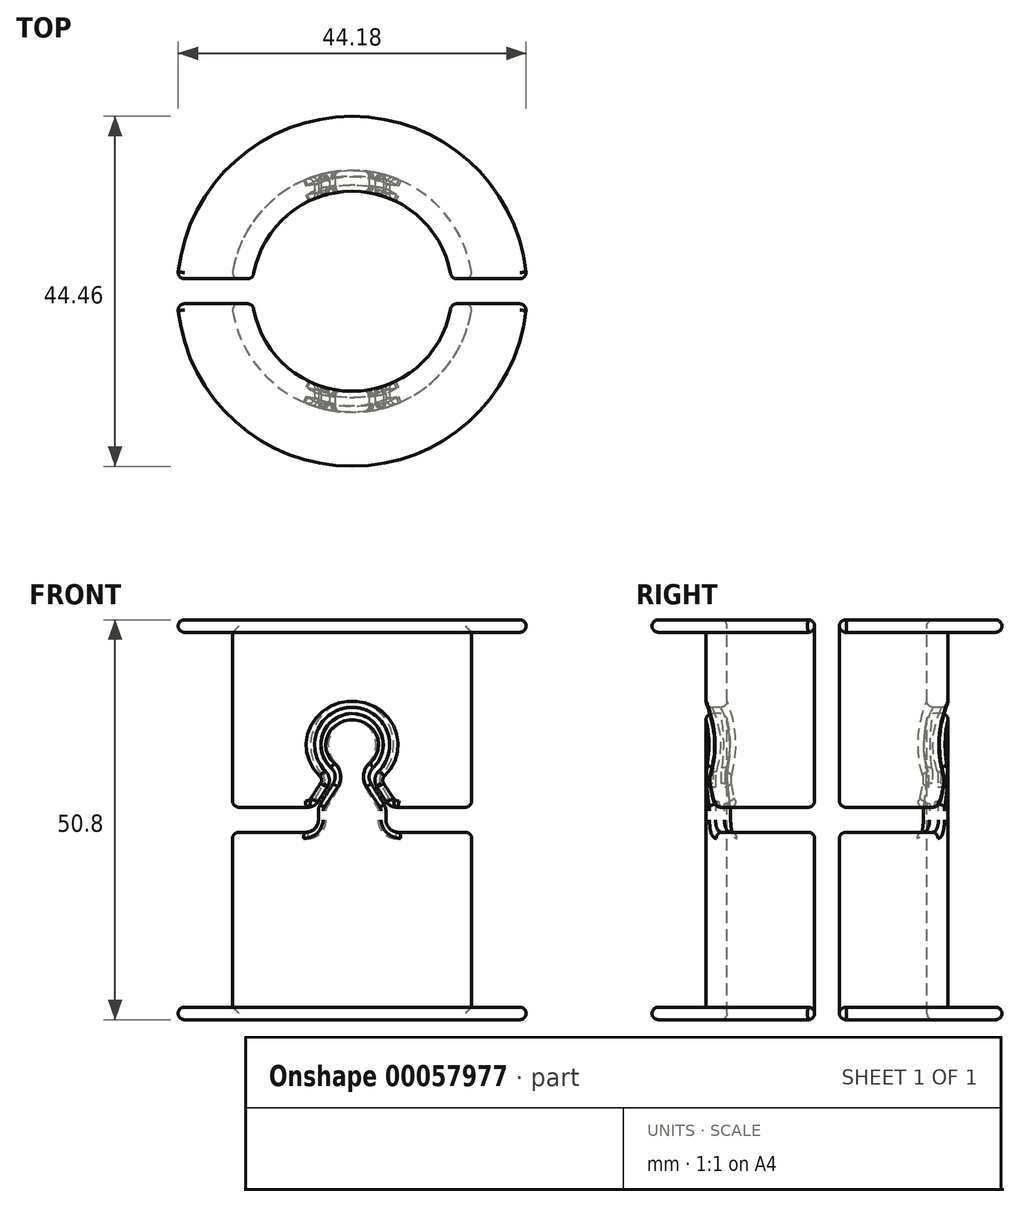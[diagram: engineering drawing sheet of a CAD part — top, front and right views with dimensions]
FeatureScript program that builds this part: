
annotation { "Feature Type Name" : "Feature", "Feature Type Description" : "" }
export const myFeature = defineFeature(function(context is Context, id is Id, definition is map)
    precondition{}
    {
        {
            var Q0;
            Q0=qCreatedBy(makeId("Right.planeOp"),FACE);
            var sketch = newSketch(context, id + "F0", { "sketchPlane" : qUnion([Q0])});
            skLineSegment(sketch, "E0", {"start": v(0, 25.4) * mm, "end": v(0, -25.4) * mm, "construction": true});
            skLineSegment(sketch, "E1", {"start": v(-13.49, 25.4) * mm, "end": v(-21.44, 25.4) * mm});
            skLineSegment(sketch, "E2", {"start": v(-22.23, 24.61) * mm, "end": v(-22.23, 24.6) * mm});
            skLineSegment(sketch, "E3", {"start": v(-21.44, 23.81) * mm, "end": v(-15.37, 23.81) * mm});
            skLineSegment(sketch, "E4", {"start": v(-15.37, 23.81) * mm, "end": v(-15.37, -23.81) * mm});
            skLineSegment(sketch, "E5", {"start": v(-15.37, -23.81) * mm, "end": v(-21.44, -23.81) * mm});
            skLineSegment(sketch, "E6", {"start": v(-22.22, -24.6) * mm, "end": v(-22.22, -24.61) * mm});
            skLineSegment(sketch, "E7", {"start": v(-21.44, -25.4) * mm, "end": v(-13.49, -25.4) * mm});
            skLineSegment(sketch, "E8", {"start": v(-12.7, 24.61) * mm, "end": v(-12.7, -24.61) * mm});
            skPoint(sketch, "E9.visualSharp", {"position": v(-12.7, 25.4) * mm});
            skArc(sketch, "E9.filletArc", {"start": v(-12.7, 24.61) * mm, "mid": v(-12.93, 25.17) * mm, "end": v(-13.49, 25.4) * mm});
            skPoint(sketch, "E10.visualSharp", {"position": v(-22.23, 25.4) * mm});
            skArc(sketch, "E10.filletArc", {"start": v(-21.44, 25.4) * mm, "mid": v(-22, 25.17) * mm, "end": v(-22.23, 24.61) * mm});
            skPoint(sketch, "E11.visualSharp", {"position": v(-22.23, 23.81) * mm});
            skArc(sketch, "E11.filletArc", {"start": v(-22.23, 24.6) * mm, "mid": v(-22, 24.04) * mm, "end": v(-21.44, 23.81) * mm});
            skPoint(sketch, "E12.visualSharp", {"position": v(-12.7, -25.4) * mm});
            skArc(sketch, "E12.filletArc", {"start": v(-13.49, -25.4) * mm, "mid": v(-12.93, -25.17) * mm, "end": v(-12.7, -24.61) * mm});
            skPoint(sketch, "E13.visualSharp", {"position": v(-22.22, -25.4) * mm});
            skArc(sketch, "E13.filletArc", {"start": v(-22.22, -24.61) * mm, "mid": v(-22, -25.17) * mm, "end": v(-21.44, -25.4) * mm});
            skPoint(sketch, "E14.visualSharp", {"position": v(-22.22, -23.81) * mm});
            skArc(sketch, "E14.filletArc", {"start": v(-21.44, -23.81) * mm, "mid": v(-22, -24.04) * mm, "end": v(-22.22, -24.6) * mm});
            skSolve(sketch);
        }
        {
            var Q0;
            Q0=makeQuery(id+"F0.imprint","IMPRINT",FACE,{"disambiguationData":[TD([[makeQuery(id+"F0.imprint","IMPRINT",EDGE,{"derivedFrom":sQuery(id+"F0.wireOp",EDGE,"E1")}),1.0]])]});
            var Q1;
            Q1=sQuery(id+"F0.wireOp",EDGE,"E0");
            revolve(context, id + "F1", {"entities" : qUnion([Q0]), "axis" : qUnion([Q1]), "revolveType" : RevolveType.FULL});
        }
        {
            var Q0;
            Q0=qCreatedBy(makeId("Top.planeOp"),FACE);
            var sketch = newSketch(context, id + "F2", { "sketchPlane" : qUnion([Q0])});
            skLineSegment(sketch, "E15.rect.bottom", {"start": v(-25.4, 1.59) * mm, "end": v(25.4, 1.59) * mm});
            skLineSegment(sketch, "E15.rect.top", {"start": v(-25.4, -1.59) * mm, "end": v(25.4, -1.59) * mm});
            skLineSegment(sketch, "E15.rect.left", {"start": v(-25.4, 1.59) * mm, "end": v(-25.4, -1.59) * mm});
            skLineSegment(sketch, "E15.rect.right", {"start": v(25.4, 1.59) * mm, "end": v(25.4, -1.59) * mm});
            skPoint(sketch, "E15.rect.middle", {"position": v(0, 0) * mm});
            skSolve(sketch);
        }
        {
            var Q0;
            Q0=qSketchRegion(id+"F2",true);
            extrude(context, id + "F3", {"entities" : qUnion([Q0]), "operationType" : NewBodyOperationType.REMOVE, "endBound" : BoundingType.SYMMETRIC, "oppositeDirection" : true, "depth" : 50.8 * mm});
        }
        {
            var Q0;
            Q0=qCreatedBy(makeId("Front.planeOp"),FACE);
            var sketch = newSketch(context, id + "F4", { "sketchPlane" : qUnion([Q0])});
            skLineSegment(sketch, "E16.rect.bottom", {"start": v(25.4, 1.59) * mm, "end": v(5.63, 1.59) * mm});
            skLineSegment(sketch, "E16.rect.top", {"start": v(25.4, -1.59) * mm, "end": v(5.86, -1.59) * mm});
            skLineSegment(sketch, "E16.rect.left", {"start": v(25.4, 1.59) * mm, "end": v(25.4, -1.59) * mm});
            skLineSegment(sketch, "E16.rect.right", {"start": v(-25.4, 1.59) * mm, "end": v(-25.4, -1.59) * mm});
            skPoint(sketch, "E16.rect.middle", {"position": v(0, 0) * mm});
            skArc(sketch, "E17", {"start": v(3.36, 6.15) * mm, "mid": v(0, 14.29) * mm, "end": v(-3.36, 6.15) * mm});
            skPoint(sketch, "E17.centerSnap0", {"position": v(0, 1.59) * mm});
            skLineSegment(sketch, "E18", {"start": v(-2.37, 5.4) * mm, "end": v(2.37, 5.4) * mm, "construction": true});
            skLineSegment(sketch, "E19", {"start": v(-4.76, 9.53) * mm, "end": v(-4.76, 1.59) * mm, "construction": true});
            skLineSegment(sketch, "E20", {"start": v(4.76, 9.53) * mm, "end": v(4.76, 1.59) * mm, "construction": true});
            skLineSegment(sketch, "E21", {"start": v(-3.13, 4.2) * mm, "end": v(-4.3, 2.33) * mm});
            skLineSegment(sketch, "E22", {"start": v(3.13, 4.2) * mm, "end": v(4.3, 2.33) * mm});
            skLineSegment(sketch, "E23.trimOffspring", {"start": v(-5.63, 1.59) * mm, "end": v(-25.4, 1.59) * mm});
            skArc(sketch, "E24", {"start": v(2.67, 6.6) * mm, "mid": v(0, 13.49) * mm, "end": v(-2.67, 6.6) * mm});
            skLineSegment(sketch, "E25", {"start": v(-1.59, 5.9) * mm, "end": v(1.59, 5.9) * mm, "construction": true});
            skLineSegment(sketch, "E26", {"start": v(-2.4, 4.6) * mm, "end": v(-4.05, 1.97) * mm});
            skLineSegment(sketch, "E27", {"start": v(-4.29, 1.13) * mm, "end": v(-4.29, -0.01) * mm});
            skLineSegment(sketch, "E28", {"start": v(2.4, 4.6) * mm, "end": v(4.05, 1.97) * mm});
            skLineSegment(sketch, "E29", {"start": v(4.29, 1.13) * mm, "end": v(4.29, -0.01) * mm});
            skLineSegment(sketch, "E30.trimOffspring", {"start": v(-5.86, -1.59) * mm, "end": v(-25.4, -1.59) * mm});
            skPoint(sketch, "E31.visualSharp", {"position": v(-1.59, 5.9) * mm});
            skArc(sketch, "E31.filletArc", {"start": v(-2.4, 4.6) * mm, "mid": v(-2.17, 5.65) * mm, "end": v(-2.67, 6.6) * mm});
            skPoint(sketch, "E32.visualSharp", {"position": v(1.59, 5.9) * mm});
            skArc(sketch, "E32.filletArc", {"start": v(2.67, 6.6) * mm, "mid": v(2.17, 5.65) * mm, "end": v(2.4, 4.6) * mm});
            skPoint(sketch, "E33.visualSharp", {"position": v(2.37, 5.4) * mm});
            skArc(sketch, "E33.filletArc", {"start": v(3.36, 6.15) * mm, "mid": v(2.9, 5.2) * mm, "end": v(3.13, 4.2) * mm});
            skPoint(sketch, "E34.visualSharp", {"position": v(-2.37, 5.4) * mm});
            skArc(sketch, "E34.filletArc", {"start": v(-3.13, 4.2) * mm, "mid": v(-2.9, 5.2) * mm, "end": v(-3.36, 6.15) * mm});
            skPoint(sketch, "E35.visualSharp", {"position": v(-4.76, 1.59) * mm});
            skArc(sketch, "E35.filletArc", {"start": v(-5.63, 1.59) * mm, "mid": v(-4.87, 1.78) * mm, "end": v(-4.3, 2.33) * mm});
            skPoint(sketch, "E36.visualSharp", {"position": v(-4.29, 1.59) * mm});
            skArc(sketch, "E36.filletArc", {"start": v(-4.05, 1.97) * mm, "mid": v(-4.23, 1.57) * mm, "end": v(-4.29, 1.13) * mm});
            skPoint(sketch, "E37.visualSharp", {"position": v(4.29, 1.59) * mm});
            skArc(sketch, "E37.filletArc", {"start": v(4.29, 1.13) * mm, "mid": v(4.23, 1.57) * mm, "end": v(4.05, 1.97) * mm});
            skPoint(sketch, "E38.visualSharp", {"position": v(4.76, 1.59) * mm});
            skArc(sketch, "E38.filletArc", {"start": v(4.3, 2.33) * mm, "mid": v(4.87, 1.78) * mm, "end": v(5.63, 1.59) * mm});
            skPoint(sketch, "E39.visualSharp", {"position": v(-4.29, -1.59) * mm});
            skArc(sketch, "E39.filletArc", {"start": v(-5.86, -1.59) * mm, "mid": v(-4.75, -1.13) * mm, "end": v(-4.29, -0.01) * mm});
            skPoint(sketch, "E40.visualSharp", {"position": v(4.29, -1.59) * mm});
            skArc(sketch, "E40.filletArc", {"start": v(4.29, -0.01) * mm, "mid": v(4.75, -1.13) * mm, "end": v(5.86, -1.59) * mm});
            skSolve(sketch);
        }
        {
            var Q0;
            Q0=makeQuery(id+"F4.imprint","IMPRINT",FACE,{"disambiguationData":[TD([[makeQuery(id+"F4.imprint","IMPRINT",EDGE,{"derivedFrom":sQuery(id+"F4.wireOp",EDGE,"E16.rect.bottom")}),1.0]])]});
            extrude(context, id + "F5", {"entities" : qUnion([Q0]), "operationType" : NewBodyOperationType.REMOVE, "endBound" : BoundingType.SYMMETRIC, "oppositeDirection" : true, "depth" : 50.8 * mm});
        }
        {
            var Q0;
            Q0=makeQuery(id+"F5.boolean.opBoolean","SPLIT",FACE,{"disambiguationData":[TD([makeQuery(id+"F1.opRevolve","SWEPT_FACE",FACE,{"disambiguationData":[OSD([sQuery(id+"F0.wireOp",EDGE,"E5")])]})])],"derivedFrom":makeQuery(id+"F3.boolean.opBoolean","COPY",FACE,{"disambiguationData":[OD(1.0)],"derivedFrom":makeQuery(id+"F3.opExtrude","SWEPT_FACE",FACE,{"disambiguationData":[OSD([sQuery(id+"F2.wireOp",EDGE,"E15.rect.bottom")])]})})});
            var Q1;
            Q1=makeQuery(id+"F5.boolean.opBoolean","SPLIT",FACE,{"disambiguationData":[TD([makeQuery(id+"F1.opRevolve","SWEPT_FACE",FACE,{"disambiguationData":[OSD([sQuery(id+"F0.wireOp",EDGE,"E1")])]})])],"derivedFrom":makeQuery(id+"F3.boolean.opBoolean","COPY",FACE,{"disambiguationData":[OD(1.0)],"derivedFrom":makeQuery(id+"F3.opExtrude","SWEPT_FACE",FACE,{"disambiguationData":[OSD([sQuery(id+"F2.wireOp",EDGE,"E15.rect.bottom")])]})})});
            var Q2;
            Q2=makeQuery(id+"F5.boolean.opBoolean","SPLIT",FACE,{"disambiguationData":[TD([makeQuery(id+"F1.opRevolve","SWEPT_FACE",FACE,{"disambiguationData":[OSD([sQuery(id+"F0.wireOp",EDGE,"E1")])]})])],"derivedFrom":makeQuery(id+"F3.boolean.opBoolean","COPY",FACE,{"disambiguationData":[OD(0.0)],"derivedFrom":makeQuery(id+"F3.opExtrude","SWEPT_FACE",FACE,{"disambiguationData":[OSD([sQuery(id+"F2.wireOp",EDGE,"E15.rect.bottom")])]})})});
            var Q3;
            Q3=makeQuery(id+"F5.boolean.opBoolean","SPLIT",FACE,{"disambiguationData":[TD([makeQuery(id+"F1.opRevolve","SWEPT_FACE",FACE,{"disambiguationData":[OSD([sQuery(id+"F0.wireOp",EDGE,"E5")])]})])],"derivedFrom":makeQuery(id+"F3.boolean.opBoolean","COPY",FACE,{"disambiguationData":[OD(0.0)],"derivedFrom":makeQuery(id+"F3.opExtrude","SWEPT_FACE",FACE,{"disambiguationData":[OSD([sQuery(id+"F2.wireOp",EDGE,"E15.rect.bottom")])]})})});
            var Q4;
            Q4=makeQuery(id+"F5.boolean.opBoolean","SPLIT",FACE,{"disambiguationData":[TD([makeQuery(id+"F1.opRevolve","SWEPT_FACE",FACE,{"disambiguationData":[OSD([sQuery(id+"F0.wireOp",EDGE,"E5")])]})])],"derivedFrom":makeQuery(id+"F3.boolean.opBoolean","COPY",FACE,{"disambiguationData":[OD(0.0)],"derivedFrom":makeQuery(id+"F3.opExtrude","SWEPT_FACE",FACE,{"disambiguationData":[OSD([sQuery(id+"F2.wireOp",EDGE,"E15.rect.top")])]})})});
            var Q5;
            Q5=makeQuery(id+"F5.boolean.opBoolean","SPLIT",FACE,{"disambiguationData":[TD([makeQuery(id+"F1.opRevolve","SWEPT_FACE",FACE,{"disambiguationData":[OSD([sQuery(id+"F0.wireOp",EDGE,"E1")])]})])],"derivedFrom":makeQuery(id+"F3.boolean.opBoolean","COPY",FACE,{"disambiguationData":[OD(0.0)],"derivedFrom":makeQuery(id+"F3.opExtrude","SWEPT_FACE",FACE,{"disambiguationData":[OSD([sQuery(id+"F2.wireOp",EDGE,"E15.rect.top")])]})})});
            var Q6;
            Q6=makeQuery(id+"F5.boolean.opBoolean","COPY",FACE,{"disambiguationData":[OD(1.0)],"derivedFrom":makeQuery(id+"F5.opExtrude","SWEPT_FACE",FACE,{"disambiguationData":[OSD([sQuery(id+"F4.wireOp",EDGE,"E30.trimOffspring")])]})});
            var Q7;
            Q7=makeQuery(id+"F5.boolean.opBoolean","COPY",FACE,{"disambiguationData":[OD(1.0)],"derivedFrom":makeQuery(id+"F5.opExtrude","SWEPT_FACE",FACE,{"disambiguationData":[OSD([sQuery(id+"F4.wireOp",EDGE,"E39.filletArc")])]})});
            var Q8;
            Q8=makeQuery(id+"F5.boolean.opBoolean","COPY",FACE,{"disambiguationData":[OD(0.0)],"derivedFrom":makeQuery(id+"F5.opExtrude","SWEPT_FACE",FACE,{"disambiguationData":[OSD([sQuery(id+"F4.wireOp",EDGE,"E30.trimOffspring")])]})});
            var Q9;
            Q9=makeQuery(id+"F5.boolean.opBoolean","COPY",FACE,{"disambiguationData":[OD(1.0)],"derivedFrom":makeQuery(id+"F5.opExtrude","SWEPT_FACE",FACE,{"disambiguationData":[OSD([sQuery(id+"F4.wireOp",EDGE,"E23.trimOffspring")])]})});
            var Q10;
            Q10=makeQuery(id+"F5.boolean.opBoolean","COPY",FACE,{"disambiguationData":[OD(0.0)],"derivedFrom":makeQuery(id+"F5.opExtrude","SWEPT_FACE",FACE,{"disambiguationData":[OSD([sQuery(id+"F4.wireOp",EDGE,"E23.trimOffspring")])]})});
            var Q11;
            Q11=makeQuery(id+"F5.boolean.opBoolean","SPLIT",FACE,{"disambiguationData":[TD([makeQuery(id+"F1.opRevolve","SWEPT_FACE",FACE,{"disambiguationData":[OSD([sQuery(id+"F0.wireOp",EDGE,"E1")])]})])],"derivedFrom":makeQuery(id+"F3.boolean.opBoolean","COPY",FACE,{"disambiguationData":[OD(1.0)],"derivedFrom":makeQuery(id+"F3.opExtrude","SWEPT_FACE",FACE,{"disambiguationData":[OSD([sQuery(id+"F2.wireOp",EDGE,"E15.rect.top")])]})})});
            var Q12;
            Q12=makeQuery(id+"F5.boolean.opBoolean","SPLIT",FACE,{"disambiguationData":[TD([makeQuery(id+"F1.opRevolve","SWEPT_FACE",FACE,{"disambiguationData":[OSD([sQuery(id+"F0.wireOp",EDGE,"E5")])]})])],"derivedFrom":makeQuery(id+"F3.boolean.opBoolean","COPY",FACE,{"disambiguationData":[OD(1.0)],"derivedFrom":makeQuery(id+"F3.opExtrude","SWEPT_FACE",FACE,{"disambiguationData":[OSD([sQuery(id+"F2.wireOp",EDGE,"E15.rect.top")])]})})});
            fillet(context, id + "F6", {"entities" : qUnion([Q0, Q1, Q2, Q3, Q4, Q5, Q6, Q7, Q8, Q9, Q10, Q11, Q12]), "radius" : 0.79 * mm, "tangentPropagation" : true, "allowEdgeOverflow" : false});
        }
    });
